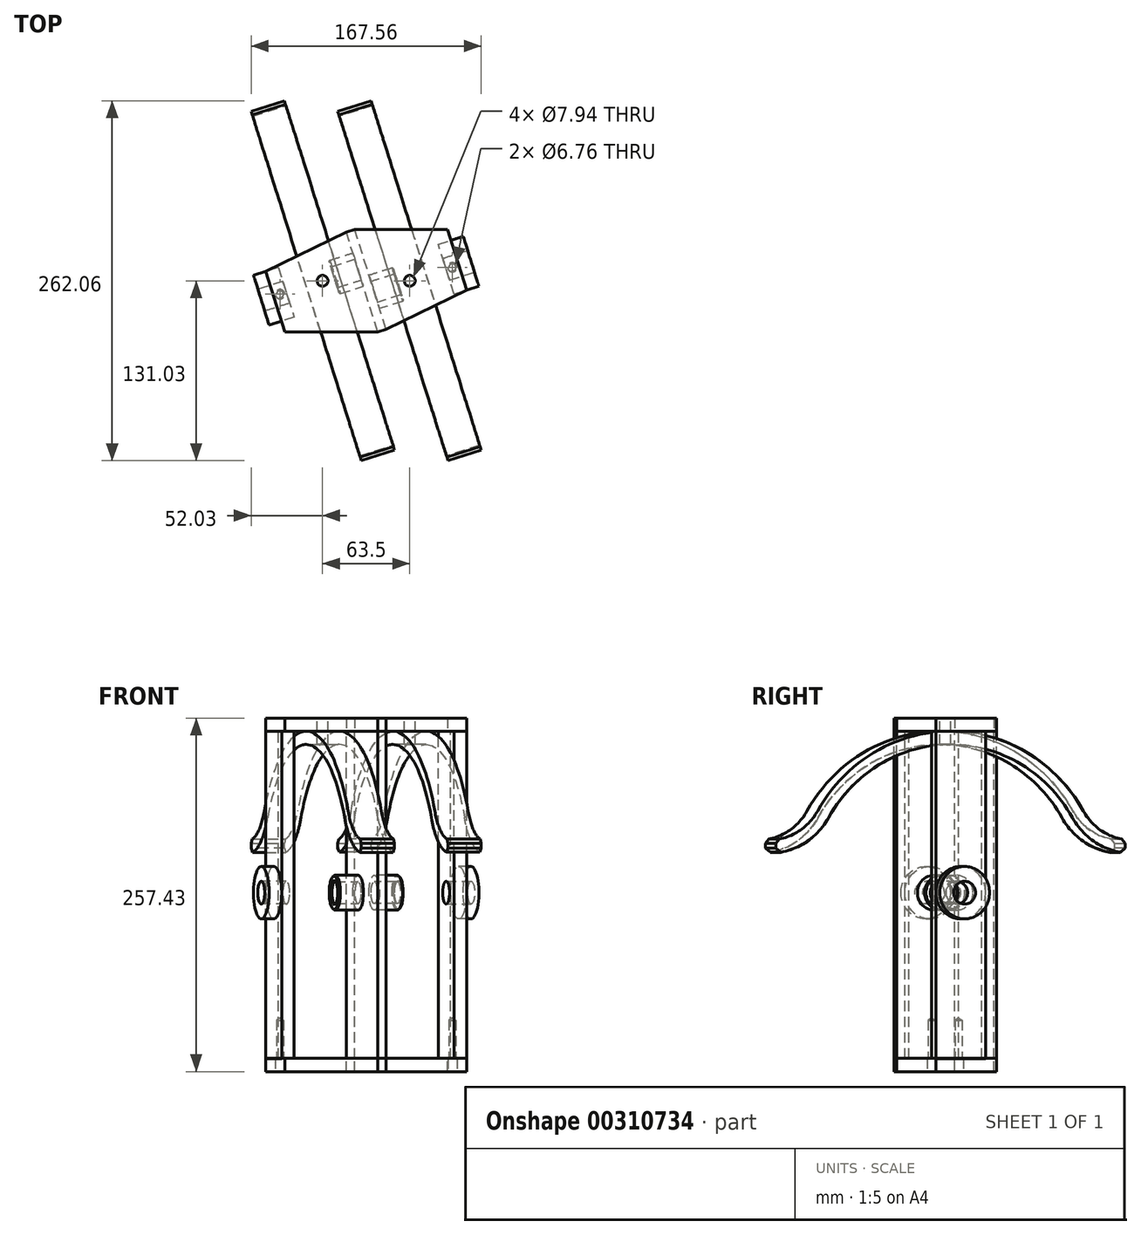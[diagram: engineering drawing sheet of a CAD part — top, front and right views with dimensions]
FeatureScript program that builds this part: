
annotation { "Feature Type Name" : "Feature", "Feature Type Description" : "" }
export const myFeature = defineFeature(function(context is Context, id is Id, definition is map)
    precondition{}
    {
        {
            var Q0;
            Q0=qCreatedBy(makeId("Top.planeOp"),FACE);
            var sketch = newSketch(context, id + "F0", { "sketchPlane" : qUnion([Q0])});
            skLineSegment(sketch, "E0", {"start": v(0, 0) * mm, "end": v(0, 62.19) * mm, "construction": true});
            skLineSegment(sketch, "E1", {"start": v(27.27, -86.5) * mm, "end": v(-20.74, 65.78) * mm, "construction": true});
            skLineSegment(sketch, "E2.0", {"start": v(-45.4, -109.41) * mm, "end": v(-93.41, 42.87) * mm, "construction": true});
            skLineSegment(sketch, "E3.0", {"start": v(14.48, -35.38) * mm, "end": v(-8.43, 37.3) * mm});
            skLineSegment(sketch, "E4", {"start": v(0, 0) * mm, "end": v(58.7, 18.5) * mm, "construction": true});
            skLineSegment(sketch, "E5.0", {"start": v(8.43, -37.3) * mm, "end": v(14.48, -35.38) * mm});
            skLineSegment(sketch, "E6.MirrorCS", {"start": v(-14.48, 35.38) * mm, "end": v(-8.43, 37.3) * mm});
            skLineSegment(sketch, "E7.MirrorCS", {"start": v(8.43, -37.3) * mm, "end": v(-14.48, 35.38) * mm});
            skPoint(sketch, "E8.orphan", {"position": v(-11.46, 36.34) * mm});
            skPoint(sketch, "E9.orphan", {"position": v(11.46, -36.34) * mm});
            skPoint(sketch, "E10.orphan", {"position": v(47.25, 54.85) * mm});
            skPoint(sketch, "E11.orphan", {"position": v(-17.71, 66.74) * mm});
            skPoint(sketch, "E12.orphan", {"position": v(-23.77, 64.83) * mm});
            skPoint(sketch, "E13.orphan", {"position": v(70.16, -17.83) * mm});
            skPoint(sketch, "E14.orphan", {"position": v(30.3, -85.54) * mm});
            skPoint(sketch, "E15.orphan", {"position": v(24.25, -87.45) * mm});
            skSolve(sketch);
        }
        {
            var Q0;
            Q0 = qSketchRegion(id + "F0", true);
            extrude(context, id + "F1", {"entities" : qUnion([Q0]), "oppositeDirection" : true, "depth" : 238.12 * mm});
        }
        {
            var Q0;
            Q0=makeQuery(id+"F1.opExtrude","SWEPT_FACE",FACE,{"disambiguationData":[OSD([sQuery(id+"F0.wireOp",EDGE,"E3.0")])]});
            var sketch = newSketch(context, id + "F2", { "sketchPlane" : qUnion([Q0])});
            skLineSegment(sketch, "E16.0", {"start": v(-38.1, 0) * mm, "end": v(38.1, 0) * mm, "construction": true});
            skLineSegment(sketch, "E17.0", {"start": v(-38.1, -117.48) * mm, "end": v(38.1, -117.48) * mm, "construction": true});
            skLineSegment(sketch, "E18", {"start": v(0, 10.84) * mm, "end": v(0, -152.28) * mm, "construction": true});
            skLineSegment(sketch, "E19.0", {"start": v(-9.53, 10.84) * mm, "end": v(-9.52, -152.28) * mm, "construction": true});
            skCircle(sketch, "E20", {"center": v(-9.52, -117.48) * mm, "radius": 12.7 * mm});
            skCircle(sketch, "E21", {"center": v(-9.52, -117.48) * mm, "radius": 7.94 * mm});
            skSolve(sketch);
        }
        {
            var Q0;
            Q0 = qSketchRegion(id + "F2", true);
            extrude(context, id + "F3", {"entities" : qUnion([Q0]), "operationType" : NewBodyOperationType.ADD, "depth" : 18.29 * mm});
        }
        {
            var Q0;
            Q0=makeQuery(id+"F3.opExtrude","CAP_FACE",FACE,{"disambiguationData":[OSD([sQuery(id+"F2.wireOp",EDGE,"E20"),sQuery(id+"F2.wireOp",EDGE,"E21")])],"isStart":false});
            chamfer(context, id + "F4", {"entities" : qUnion([Q0]), "width" : 0.76 * mm, "tangentPropagation" : true});
        }
        {
            var Q0;
            Q0=makeQuery(id+"F1.opExtrude","SWEPT_FACE",FACE,{"disambiguationData":[OSD([sQuery(id+"F0.wireOp",EDGE,"E7.MirrorCS")])]});
            var sketch = newSketch(context, id + "F5", { "sketchPlane" : qUnion([Q0])});
            skLineSegment(sketch, "E22", {"start": v(0, 41.67) * mm, "end": v(0, -224.56) * mm, "construction": true});
            skCircle(sketch, "E23.0", {"center": v(9.52, -117.48) * mm, "radius": 12.7 * mm, "construction": true});
            skCircle(sketch, "E24.0", {"center": v(9.52, -117.48) * mm, "radius": 7.94 * mm, "construction": true});
            skCircle(sketch, "E25.MirrorC", {"center": v(-9.52, -117.48) * mm, "radius": 12.7 * mm});
            skCircle(sketch, "E26.MirrorC", {"center": v(-9.52, -117.48) * mm, "radius": 7.94 * mm});
            skSolve(sketch);
        }
        {
            var Q0;
            Q0 = qSketchRegion(id + "F5", true);
            extrude(context, id + "F6", {"entities" : qUnion([Q0]), "operationType" : NewBodyOperationType.ADD, "depth" : 18.29 * mm});
        }
        {
            var Q0;
            Q0=makeQuery(id+"F6.opExtrude","CAP_FACE",FACE,{"disambiguationData":[OSD([sQuery(id+"F5.wireOp",EDGE,"E25.MirrorC"),sQuery(id+"F5.wireOp",EDGE,"E26.MirrorC")])],"isStart":false});
            chamfer(context, id + "F7", {"entities" : qUnion([Q0]), "width" : 0.76 * mm, "tangentPropagation" : true});
        }
        {
            var Q0;
            Q0=makeQuery(id+"F1.opExtrude","CAP_FACE",FACE,{"disambiguationData":[OSD([sQuery(id+"F0.wireOp",EDGE,"E3.0"),sQuery(id+"F0.wireOp",EDGE,"E5.0"),sQuery(id+"F0.wireOp",EDGE,"E6.MirrorCS"),sQuery(id+"F0.wireOp",EDGE,"E7.MirrorCS")])],"isStart":true});
            var sketch = newSketch(context, id + "F8", { "sketchPlane" : qUnion([Q0])});
            skLineSegment(sketch, "E27.0.0", {"start": v(-14.48, 35.38) * mm, "end": v(8.43, -37.3) * mm, "construction": true});
            skLineSegment(sketch, "E27.0.1", {"start": v(8.43, -37.3) * mm, "end": v(14.48, -35.38) * mm, "construction": true});
            skLineSegment(sketch, "E27.0.2", {"start": v(14.48, -35.38) * mm, "end": v(-8.43, 37.3) * mm, "construction": true});
            skLineSegment(sketch, "E27.0.3", {"start": v(-8.43, 37.3) * mm, "end": v(-14.48, 35.38) * mm, "construction": true});
            skLineSegment(sketch, "E28.0", {"start": v(63.95, -9.8) * mm, "end": v(52.49, 26.54) * mm});
            skLineSegment(sketch, "E29.0", {"start": v(73.03, -6.94) * mm, "end": v(61.57, 29.4) * mm});
            skLineSegment(sketch, "E30", {"start": v(3.59, 4.46) * mm, "end": v(18.85, 9.27) * mm, "construction": true});
            skLineSegment(sketch, "E31", {"start": v(26.49, -14.95) * mm, "end": v(11.23, -19.76) * mm, "construction": true});
            skLineSegment(sketch, "E32", {"start": v(11.22, 6.87) * mm, "end": v(18.86, -17.36) * mm, "construction": true});
            skLineSegment(sketch, "E33", {"start": v(15.04, -5.25) * mm, "end": v(104, 22.8) * mm, "construction": true});
            skLineSegment(sketch, "E34.0", {"start": v(63.95, -9.8) * mm, "end": v(73.03, -6.94) * mm});
            skLineSegment(sketch, "E35.MirrorCS", {"start": v(52.49, 26.54) * mm, "end": v(61.57, 29.4) * mm});
            skPoint(sketch, "E36.orphan", {"position": v(9.3, 12.92) * mm});
            skPoint(sketch, "E37.orphan", {"position": v(20.77, -23.41) * mm});
            skPoint(sketch, "E38.orphan", {"position": v(98.28, 40.97) * mm});
            skPoint(sketch, "E39.orphan", {"position": v(109.74, 4.64) * mm});
            skLineSegment(sketch, "E40.0", {"start": v(-63.95, 9.8) * mm, "end": v(-52.49, -26.54) * mm});
            skLineSegment(sketch, "E41", {"start": v(-26.49, 14.95) * mm, "end": v(-11.23, 19.76) * mm, "construction": true});
            skLineSegment(sketch, "E42", {"start": v(-3.59, -4.46) * mm, "end": v(-18.85, -9.27) * mm, "construction": true});
            skLineSegment(sketch, "E43", {"start": v(-18.86, 17.36) * mm, "end": v(-11.22, -6.87) * mm, "construction": true});
            skLineSegment(sketch, "E44", {"start": v(-15.04, 5.25) * mm, "end": v(-81.51, -15.71) * mm, "construction": true});
            skLineSegment(sketch, "E45.0", {"start": v(-73.03, 6.94) * mm, "end": v(-61.57, -29.4) * mm});
            skLineSegment(sketch, "E46.0", {"start": v(-63.95, 9.8) * mm, "end": v(-73.03, 6.94) * mm});
            skLineSegment(sketch, "E47.MirrorCS", {"start": v(-52.49, -26.54) * mm, "end": v(-61.57, -29.4) * mm});
            skPoint(sketch, "E48.orphan", {"position": v(-20.77, 23.41) * mm});
            skPoint(sketch, "E49.orphan", {"position": v(-9.3, -12.92) * mm});
            skPoint(sketch, "E50.orphan", {"position": v(-75.78, -33.88) * mm});
            skPoint(sketch, "E51.orphan", {"position": v(-87.24, 2.45) * mm});
            skSolve(sketch);
        }
        {
            var Q0;
            Q0=makeQuery(id+"F8.imprint","IMPRINT",FACE,{"disambiguationData":[TD([[makeQuery(id+"F8.imprint","IMPRINT",EDGE,{"derivedFrom":sQuery(id+"F8.wireOp",EDGE,"E40.0")}),-1.0]])]});
            var Q1;
            Q1=makeQuery(id+"F8.imprint","IMPRINT",FACE,{"disambiguationData":[TD([[makeQuery(id+"F8.imprint","IMPRINT",EDGE,{"derivedFrom":sQuery(id+"F8.wireOp",EDGE,"E28.0")}),-1.0]])]});
            var Q2;
            Q2 = qConstructionFilter(qBodyType(qCreatedBy(id + "F8" ,EDGE), BodyType.WIRE), ConstructionObject.NO);
            extrude(context, id + "F9", {"entities" : qUnion([Q0, Q1]), "surfaceEntities" : qUnion([Q2]), "oppositeDirection" : true, "depth" : 238.25 * mm});
        }
        {
            var Q0;
            Q0=makeQuery(id+"F9.opExtrude","SWEPT_FACE",FACE,{"disambiguationData":[OSD([sQuery(id+"F8.wireOp",EDGE,"E29.0")])]});
            var sketch = newSketch(context, id + "F10", { "sketchPlane" : qUnion([Q0])});
            skCircle(sketch, "E52.0.0", {"center": v(-9.52, -117.48) * mm, "radius": 11.94 * mm, "construction": true});
            skSolve(sketch);
        }
        {
            var Q0;
            Q0=sQuery(id+"F10.wireOp",VERTEX,"E52.0.0.center");
            var Q1;
            Q1=makeQuery(id+"F9.opExtrude","SWEPT_BODY",BODY,{"disambiguationData":[OSD([sQuery(id+"F8.wireOp",EDGE,"E28.0"),sQuery(id+"F8.wireOp",EDGE,"E29.0"),sQuery(id+"F8.wireOp",EDGE,"E34.0"),sQuery(id+"F8.wireOp",EDGE,"E35.MirrorCS")])]});
            hole(context, id + "F11", {"style" : HoleStyle.SIMPLE, "endStyle" : HoleEndStyle.BLIND, "standardTappedOrClearance" : lookupTablePath({ "standard" : "ANSI", "engagement" : "75%", "pitch" : "10 tpi", "size" : "3/4", "type" : "Tapped" }), "standardBlindInLast" : lookupTablePath({ "standard" : "ANSI", "engagement" : "75%", "pitch" : "10 tpi", "size" : "3/4", "type" : "Tapped" }), "holeDiameter" : 16.67 * mm, "showTappedDepth" : true, "holeDepth" : 31.75 * mm, "tappedDepth" : 24.13 * mm, "tapClearance" : 3, "startFromSketch" : true, "locations" : qUnion([Q0]), "scope" : qUnion([Q1]), "majorDiameter" : 19.05 * mm});
        }
        {
            var Q0;
            Q0=makeQuery(id+"F9.opExtrude","SWEPT_FACE",FACE,{"disambiguationData":[OSD([sQuery(id+"F8.wireOp",EDGE,"E45.0")])]});
            var sketch = newSketch(context, id + "F12", { "sketchPlane" : qUnion([Q0])});
            skCircle(sketch, "E53.0.0", {"center": v(-9.52, -117.48) * mm, "radius": 11.94 * mm, "construction": true});
            skSolve(sketch);
        }
        {
            var Q0;
            Q0=sQuery(id+"F12.wireOp",VERTEX,"E53.0.0.center");
            var Q1;
            Q1=makeQuery(id+"F9.opExtrude","SWEPT_BODY",BODY,{"disambiguationData":[OSD([sQuery(id+"F8.wireOp",EDGE,"E40.0"),sQuery(id+"F8.wireOp",EDGE,"E45.0"),sQuery(id+"F8.wireOp",EDGE,"E46.0"),sQuery(id+"F8.wireOp",EDGE,"E47.MirrorCS")])]});
            hole(context, id + "F13", {"style" : HoleStyle.SIMPLE, "endStyle" : HoleEndStyle.BLIND, "standardTappedOrClearance" : lookupTablePath({ "standard" : "ANSI", "engagement" : "75%", "pitch" : "10 tpi", "size" : "3/4", "type" : "Tapped" }), "standardBlindInLast" : lookupTablePath({ "standard" : "ANSI", "engagement" : "75%", "pitch" : "10 tpi", "size" : "3/4", "type" : "Tapped" }), "holeDiameter" : 16.67 * mm, "showTappedDepth" : true, "holeDepth" : 31.75 * mm, "tappedDepth" : 24.13 * mm, "tapClearance" : 3, "startFromSketch" : true, "locations" : qUnion([Q0]), "scope" : qUnion([Q1]), "majorDiameter" : 19.05 * mm});
        }
        {
            var Q0;
            Q0=makeQuery(id+"F1.opExtrude","CAP_FACE",FACE,{"disambiguationData":[OSD([sQuery(id+"F0.wireOp",EDGE,"E3.0"),sQuery(id+"F0.wireOp",EDGE,"E5.0"),sQuery(id+"F0.wireOp",EDGE,"E6.MirrorCS"),sQuery(id+"F0.wireOp",EDGE,"E7.MirrorCS")])],"isStart":true});
            var sketch = newSketch(context, id + "F14", { "sketchPlane" : qUnion([Q0])});
            skLineSegment(sketch, "E54.0.1", {"start": v(8.43, -37.3) * mm, "end": v(14.48, -35.38) * mm});
            skLineSegment(sketch, "E54.0.3", {"start": v(-8.43, 37.3) * mm, "end": v(-14.48, 35.38) * mm});
            skLineSegment(sketch, "E55.0.1", {"start": v(-73.03, 6.94) * mm, "end": v(-59.08, -37.3) * mm});
            skLineSegment(sketch, "E56.0.1", {"start": v(73.03, -6.94) * mm, "end": v(59.08, 37.3) * mm});
            skPoint(sketch, "E55.0.3.end.orphan", {"position": v(-63.95, 9.8) * mm});
            skPoint(sketch, "E55.0.2.end.orphan", {"position": v(-52.49, -26.54) * mm});
            skPoint(sketch, "E56.0.3.end.orphan", {"position": v(63.95, -9.8) * mm});
            skPoint(sketch, "E56.0.3.start.orphan", {"position": v(52.49, 26.54) * mm});
            skPoint(sketch, "E57.orphan", {"position": v(-8.43, 37.3) * mm});
            skPoint(sketch, "E58.orphan", {"position": v(-14.48, 35.38) * mm});
            skPoint(sketch, "E59.orphan", {"position": v(8.43, -37.3) * mm});
            skPoint(sketch, "E60.orphan", {"position": v(14.48, -35.38) * mm});
            skPoint(sketch, "E61.orphan", {"position": v(-61.57, -29.4) * mm});
            skPoint(sketch, "E62.orphan", {"position": v(-73.03, 6.94) * mm});
            skPoint(sketch, "E63.orphan", {"position": v(61.57, 29.4) * mm});
            skPoint(sketch, "E64.orphan", {"position": v(73.03, -6.94) * mm});
            skLineSegment(sketch, "E65", {"start": v(14.48, -35.38) * mm, "end": v(73.03, -6.94) * mm});
            skLineSegment(sketch, "E66", {"start": v(-14.48, 35.38) * mm, "end": v(-73.03, 6.94) * mm});
            skLineSegment(sketch, "E67", {"start": v(8.43, -37.3) * mm, "end": v(-59.08, -37.3) * mm});
            skLineSegment(sketch, "E68", {"start": v(-8.43, 37.3) * mm, "end": v(59.08, 37.3) * mm});
            skSolve(sketch);
        }
        {
            var Q0;
            Q0 = qSketchRegion(id + "F14", true);
            extrude(context, id + "F15", {"entities" : qUnion([Q0]), "depth" : 9.65 * mm});
        }
        {
            var Q0;
            Q0=makeQuery(id+"F15.opExtrude","CAP_FACE",FACE,{"disambiguationData":[OSD([sQuery(id+"F14.wireOp",EDGE,"E54.0.1"),sQuery(id+"F14.wireOp",EDGE,"E54.0.3"),sQuery(id+"F14.wireOp",EDGE,"E55.0.1"),sQuery(id+"F14.wireOp",EDGE,"E56.0.1"),sQuery(id+"F14.wireOp",EDGE,"E65"),sQuery(id+"F14.wireOp",EDGE,"E66"),sQuery(id+"F14.wireOp",EDGE,"E67"),sQuery(id+"F14.wireOp",EDGE,"E68")])],"isStart":false});
            var sketch = newSketch(context, id + "F16", { "sketchPlane" : qUnion([Q0])});
            skLineSegment(sketch, "E69", {"start": v(-60.86, 0) * mm, "end": v(-22.5, 0) * mm, "construction": true});
            skLineSegment(sketch, "E70.0", {"start": v(-63.95, 9.8) * mm, "end": v(-52.49, -26.54) * mm, "construction": true});
            skLineSegment(sketch, "E71.0", {"start": v(-19.74, -8.76) * mm, "end": v(-26.92, 14.02) * mm, "construction": true});
            skLineSegment(sketch, "E72.0", {"start": v(19.74, 8.76) * mm, "end": v(26.92, -14.02) * mm, "construction": true});
            skLineSegment(sketch, "E73.0", {"start": v(63.95, -9.8) * mm, "end": v(52.49, 26.54) * mm, "construction": true});
            skLineSegment(sketch, "E74.trimOffspring", {"start": v(22.5, 0) * mm, "end": v(60.86, 0) * mm, "construction": true});
            skPoint(sketch, "E75.orphan", {"position": v(-89.3, 0) * mm});
            skPoint(sketch, "E76", {"position": v(-41.68, 0) * mm});
            skPoint(sketch, "E77", {"position": v(41.68, 0) * mm});
            skLineSegment(sketch, "E78.0", {"start": v(8.43, -37.3) * mm, "end": v(-14.48, 35.38) * mm, "construction": true});
            skLineSegment(sketch, "E79", {"start": v(-9.78, 20.47) * mm, "end": v(-108.3, -10.59) * mm, "construction": true});
            skSolve(sketch);
        }
        {
            var Q0;
            {var subQ1=sQuery(id+"F0.wireOp",EDGE,"E5.0");var subQ2=sQuery(id+"F0.wireOp",EDGE,"E7.MirrorCS");Q0=makeQuery(id+"F6.boolean.opBoolean","SPLIT",FACE,{"disambiguationData":[TD([makeQuery(id+"F1.opExtrude","SWEPT_FACE",FACE,{"disambiguationData":[OSD([subQ1])]})])],"derivedFrom":makeQuery(id+"F1.opExtrude","SWEPT_FACE",FACE,{"disambiguationData":[OSD([subQ2])]})});}
            cPlane(context, id + "F17", {"entities" : qUnion([Q0]), "cplaneType" : CPlaneType.OFFSET, "offset" : 26.92 * mm, "width" : 152.4 * mm, "height" : 152.4 * mm});
        }
        {
            var Q0;
            Q0=qCreatedBy(id+"F17.planeOp",FACE);
            var sketch = newSketch(context, id + "F18", { "sketchPlane" : qUnion([Q0])});
            skCircle(sketch, "E80.0.0", {"center": v(-9.52, -117.48) * mm, "radius": 11.94 * mm, "construction": true});
            skArc(sketch, "E81", {"start": v(83.63, -62.93) * mm, "mid": v(-9.53, -9.53) * mm, "end": v(-102.68, -62.93) * mm});
            skLineSegment(sketch, "E82", {"start": v(-9.52, -117.48) * mm, "end": v(-9.52, -9.53) * mm, "construction": true});
            skLineSegment(sketch, "E83", {"start": v(-9.52, -9.53) * mm, "end": v(-163.72, -9.53) * mm, "construction": true});
            skLineSegment(sketch, "E84.0", {"start": v(104.55, -88.9) * mm, "end": v(-142.88, -88.9) * mm, "construction": true});
            skLineSegment(sketch, "E85.0", {"start": v(-9.52, -36.58) * mm, "end": v(-163.72, -36.58) * mm, "construction": true});
            skLineSegment(sketch, "E86.0", {"start": v(-147.7, -117.48) * mm, "end": v(-147.7, -9.53) * mm, "construction": true});
            skArc(sketch, "E87", {"start": v(-147.7, -88.74) * mm, "mid": v(-121.76, -81.83) * mm, "end": v(-102.68, -62.93) * mm});
            skArc(sketch, "E88", {"start": v(-142.88, -78.82) * mm, "mid": v(-124.5, -72.2) * mm, "end": v(-111.01, -58.06) * mm});
            skArc(sketch, "E89.trimOffspring", {"start": v(-95.54, -37.28) * mm, "mid": v(-95.54, -36.93) * mm, "end": v(-95.53, -36.58) * mm});
            skLineSegment(sketch, "E90.0", {"start": v(-142.88, -88.9) * mm, "end": v(-142.88, -78.82) * mm});
            skLineSegment(sketch, "E91.trimOffspring", {"start": v(-142.88, -36.58) * mm, "end": v(-142.88, -9.53) * mm});
            skLineSegment(sketch, "E92.trimOffspring", {"start": v(-147.7, -88.9) * mm, "end": v(-163.72, -88.9) * mm, "construction": true});
            skLineSegment(sketch, "E93.MirrorCS", {"start": v(123.83, -88.9) * mm, "end": v(123.83, -78.82) * mm});
            skArc(sketch, "E94.MirrorCS", {"start": v(128.65, -88.74) * mm, "mid": v(102.7, -81.83) * mm, "end": v(83.63, -62.93) * mm});
            skLineSegment(sketch, "E95.MirrorCS", {"start": v(128.65, -88.9) * mm, "end": v(144.67, -88.9) * mm, "construction": true});
            skArc(sketch, "E96.MirrorCS", {"start": v(123.83, -78.82) * mm, "mid": v(105.44, -72.2) * mm, "end": v(91.96, -58.06) * mm});
            skArc(sketch, "E97.trimOffspring", {"start": v(91.96, -58.06) * mm, "mid": v(-9.53, 0.13) * mm, "end": v(-111.01, -58.06) * mm});
            skSolve(sketch);
        }
        {
            var Q0;
            Q0 = qSketchRegion(id + "F18", true);
            extrude(context, id + "F19", {"entities" : qUnion([Q0]), "endBound" : BoundingType.SYMMETRIC, "depth" : 25.4 * mm});
        }
        {
            var Q0;
            Q0=makeQuery(id+"F19.opExtrude","SWEPT_EDGE",EDGE,{"disambiguationData":[OSD([sQuery(id+"F18.wireOp",EDGE,"E93.MirrorCS"),sQuery(id+"F18.wireOp",EDGE,"E96.MirrorCS")])]});
            var Q1;
            Q1=makeQuery(id+"F19.opExtrude","SWEPT_EDGE",EDGE,{"disambiguationData":[OSD([sQuery(id+"F18.wireOp",EDGE,"E93.MirrorCS"),sQuery(id+"F18.wireOp",EDGE,"E94.MirrorCS")])]});
            var Q2;
            Q2=makeQuery(id+"F19.opExtrude","SWEPT_EDGE",EDGE,{"disambiguationData":[OSD([sQuery(id+"F18.wireOp",EDGE,"E87"),sQuery(id+"F18.wireOp",EDGE,"E90.0")])]});
            var Q3;
            Q3=makeQuery(id+"F19.opExtrude","SWEPT_EDGE",EDGE,{"disambiguationData":[OSD([sQuery(id+"F18.wireOp",EDGE,"E88"),sQuery(id+"F18.wireOp",EDGE,"E90.0")])]});
            chamfer(context, id + "F20", {"entities" : qUnion([Q0, Q1, Q2, Q3]), "width" : 3.17 * mm, "tangentPropagation" : true});
        }
        {
            var Q0;
            {var subQ1=sQuery(id+"F0.wireOp",EDGE,"E5.0");var subQ3=sQuery(id+"F0.wireOp",EDGE,"E3.0");Q0=makeQuery(id+"F3.boolean.opBoolean","SPLIT",FACE,{"disambiguationData":[TD([makeQuery(id+"F1.opExtrude","SWEPT_FACE",FACE,{"disambiguationData":[OSD([subQ1])]})])],"derivedFrom":makeQuery(id+"F1.opExtrude","SWEPT_FACE",FACE,{"disambiguationData":[OSD([subQ3])]})});}
            cPlane(context, id + "F21", {"entities" : qUnion([Q0]), "cplaneType" : CPlaneType.OFFSET, "offset" : 26.92 * mm, "width" : 152.4 * mm, "height" : 152.4 * mm});
        }
        {
            var Q0;
            Q0=qCreatedBy(id+"F21.planeOp",FACE);
            var sketch = newSketch(context, id + "F22", { "sketchPlane" : qUnion([Q0])});
            skCircle(sketch, "E98.0", {"center": v(-9.52, -117.48) * mm, "radius": 12.7 * mm, "construction": true});
            skArc(sketch, "E99", {"start": v(83.61, -62.9) * mm, "mid": v(-9.52, -9.52) * mm, "end": v(-102.66, -62.9) * mm});
            skArc(sketch, "E100.0", {"start": v(104.55, -88.9) * mm, "mid": v(103.58, -85.27) * mm, "end": v(102.5, -81.68) * mm});
            skLineSegment(sketch, "E101", {"start": v(-9.52, -117.48) * mm, "end": v(-9.52, -9.53) * mm, "construction": true});
            skLineSegment(sketch, "E102", {"start": v(-9.52, -9.53) * mm, "end": v(180.2, -9.53) * mm, "construction": true});
            skLineSegment(sketch, "E103.0", {"start": v(-9.52, -88.9) * mm, "end": v(180.2, -88.9) * mm, "construction": true});
            skLineSegment(sketch, "E104.0", {"start": v(-9.52, -36.5) * mm, "end": v(180.2, -36.5) * mm, "construction": true});
            skLineSegment(sketch, "E105.0", {"start": v(128.65, -117.48) * mm, "end": v(128.65, -9.53) * mm, "construction": true});
            skArc(sketch, "E106", {"start": v(173.35, -9.53) * mm, "mid": v(114.3, 13.7) * mm, "end": v(76.45, -37.24) * mm});
            skArc(sketch, "E107", {"start": v(171.2, -36.5) * mm, "mid": v(142.97, 3.57) * mm, "end": v(95.74, -9.53) * mm});
            skLineSegment(sketch, "E108.0", {"start": v(123.83, -117.48) * mm, "end": v(123.83, -9.53) * mm});
            skArc(sketch, "E109.trimOffspring", {"start": v(91.94, -58.01) * mm, "mid": v(105.43, -72.16) * mm, "end": v(123.83, -78.78) * mm});
            skArc(sketch, "E110.trimOffspring", {"start": v(83.61, -62.9) * mm, "mid": v(102.7, -81.8) * mm, "end": v(128.65, -88.7) * mm});
            skArc(sketch, "E111.MirrorCS", {"start": v(-110.99, -58.01) * mm, "mid": v(-124.48, -72.16) * mm, "end": v(-142.88, -78.78) * mm});
            skArc(sketch, "E112.MirrorCS", {"start": v(-102.66, -62.9) * mm, "mid": v(-119.68, -80.55) * mm, "end": v(-142.88, -88.48) * mm});
            skLineSegment(sketch, "E113.MirrorCS", {"start": v(-142.88, -88.48) * mm, "end": v(-142.88, -78.78) * mm});
            skPoint(sketch, "E114.orphan", {"position": v(-142.88, -9.53) * mm});
            skPoint(sketch, "E115.orphan", {"position": v(-147.7, -88.7) * mm});
            skPoint(sketch, "E116.orphan", {"position": v(-142.88, -117.48) * mm});
            skArc(sketch, "E117.trimOffspring", {"start": v(91.94, -58.01) * mm, "mid": v(-9.52, 0.13) * mm, "end": v(-110.99, -58.01) * mm});
            skSolve(sketch);
        }
        {
            var Q0;
            Q0 = qSketchRegion(id + "F22", true);
            extrude(context, id + "F23", {"entities" : qUnion([Q0]), "endBound" : BoundingType.SYMMETRIC, "depth" : 25.4 * mm});
        }
        {
            var Q0;
            Q0=makeQuery(id+"F23.opExtrude","SWEPT_EDGE",EDGE,{"disambiguationData":[OSD([sQuery(id+"F22.wireOp",EDGE,"E108.0"),sQuery(id+"F22.wireOp",EDGE,"E109.trimOffspring")])]});
            var Q1;
            Q1=makeQuery(id+"F23.opExtrude","SWEPT_EDGE",EDGE,{"disambiguationData":[OSD([sQuery(id+"F22.wireOp",EDGE,"E108.0"),sQuery(id+"F22.wireOp",EDGE,"E110.trimOffspring")])]});
            var Q2;
            Q2=makeQuery(id+"F23.opExtrude","SWEPT_EDGE",EDGE,{"disambiguationData":[OSD([sQuery(id+"F22.wireOp",EDGE,"E111.MirrorCS"),sQuery(id+"F22.wireOp",EDGE,"E113.MirrorCS")])]});
            var Q3;
            Q3=makeQuery(id+"F23.opExtrude","SWEPT_EDGE",EDGE,{"disambiguationData":[OSD([sQuery(id+"F22.wireOp",EDGE,"E112.MirrorCS"),sQuery(id+"F22.wireOp",EDGE,"E113.MirrorCS")])]});
            chamfer(context, id + "F24", {"entities" : qUnion([Q0, Q1, Q2, Q3]), "width" : 3.17 * mm, "tangentPropagation" : true});
        }
        {
            var Q0;
            Q0=makeQuery(id+"F1.opExtrude","CAP_FACE",FACE,{"disambiguationData":[OSD([sQuery(id+"F0.wireOp",EDGE,"E3.0"),sQuery(id+"F0.wireOp",EDGE,"E5.0"),sQuery(id+"F0.wireOp",EDGE,"E6.MirrorCS"),sQuery(id+"F0.wireOp",EDGE,"E7.MirrorCS")])],"isStart":false});
            var sketch = newSketch(context, id + "F25", { "sketchPlane" : qUnion([Q0])});
            skLineSegment(sketch, "E118.0.0", {"start": v(-59.08, 37.3) * mm, "end": v(8.43, 37.3) * mm});
            skLineSegment(sketch, "E118.0.1", {"start": v(8.43, 37.3) * mm, "end": v(14.48, 35.38) * mm});
            skLineSegment(sketch, "E118.0.2", {"start": v(14.48, 35.38) * mm, "end": v(73.03, 6.94) * mm});
            skLineSegment(sketch, "E118.0.3", {"start": v(73.03, 6.94) * mm, "end": v(59.08, -37.3) * mm});
            skLineSegment(sketch, "E118.0.4", {"start": v(59.08, -37.3) * mm, "end": v(-8.43, -37.3) * mm});
            skLineSegment(sketch, "E118.0.5", {"start": v(-8.43, -37.3) * mm, "end": v(-14.48, -35.38) * mm});
            skLineSegment(sketch, "E118.0.6", {"start": v(-14.48, -35.38) * mm, "end": v(-73.03, -6.94) * mm});
            skLineSegment(sketch, "E118.0.7", {"start": v(-73.03, -6.94) * mm, "end": v(-59.08, 37.3) * mm});
            skSolve(sketch);
        }
        {
            var Q0;
            Q0 = qSketchRegion(id + "F25", true);
            extrude(context, id + "F26", {"entities" : qUnion([Q0]), "depth" : 9.65 * mm});
        }
        {
            var Q0;
            Q0=makeQuery(id+"F9.opExtrude","CAP_FACE",FACE,{"disambiguationData":[OSD([sQuery(id+"F8.wireOp",EDGE,"E40.0"),sQuery(id+"F8.wireOp",EDGE,"E45.0"),sQuery(id+"F8.wireOp",EDGE,"E46.0"),sQuery(id+"F8.wireOp",EDGE,"E47.MirrorCS")])],"isStart":false});
            var sketch = newSketch(context, id + "F27", { "sketchPlane" : qUnion([Q0])});
            skLineSegment(sketch, "E119.0.0", {"start": v(-73.03, -6.94) * mm, "end": v(-63.95, -9.8) * mm, "construction": true});
            skLineSegment(sketch, "E119.0.1", {"start": v(-63.95, -9.8) * mm, "end": v(-52.49, 26.54) * mm, "construction": true});
            skLineSegment(sketch, "E119.0.2", {"start": v(-52.49, 26.54) * mm, "end": v(-61.57, 29.4) * mm, "construction": true});
            skLineSegment(sketch, "E119.0.3", {"start": v(-61.57, 29.4) * mm, "end": v(-73.03, -6.94) * mm, "construction": true});
            skLineSegment(sketch, "E120", {"start": v(-73.03, -6.94) * mm, "end": v(-52.49, 26.54) * mm, "construction": true});
            skPoint(sketch, "E121", {"position": v(-62.76, 9.8) * mm});
            skSolve(sketch);
        }
        {
            var Q0;
            Q0=sQuery(id+"F27.wireOp",VERTEX,"E121");
            var Q1;
            Q1=makeQuery(id+"F9.opExtrude","SWEPT_BODY",BODY,{"disambiguationData":[OSD([sQuery(id+"F8.wireOp",EDGE,"E40.0"),sQuery(id+"F8.wireOp",EDGE,"E45.0"),sQuery(id+"F8.wireOp",EDGE,"E46.0"),sQuery(id+"F8.wireOp",EDGE,"E47.MirrorCS")])]});
            hole(context, id + "F28", {"style" : HoleStyle.SIMPLE, "endStyle" : HoleEndStyle.BLIND, "standardTappedOrClearance" : lookupTablePath({ "standard" : "ANSI", "engagement" : "75%", "pitch" : "20 tpi", "size" : "1/4", "type" : "Tapped" }), "standardBlindInLast" : lookupTablePath({ "standard" : "ANSI", "engagement" : "75%", "pitch" : "20 tpi", "size" : "1/4", "type" : "Tapped" }), "holeDiameter" : 5.1 * mm, "showTappedDepth" : true, "holeDepth" : 27.94 * mm, "tappedDepth" : 24.13 * mm, "tapClearance" : 3, "startFromSketch" : true, "locations" : qUnion([Q0]), "scope" : qUnion([Q1]), "majorDiameter" : 6.35 * mm});
        }
        {
            var Q0;
            Q0=makeQuery(id+"F9.opExtrude","CAP_FACE",FACE,{"disambiguationData":[OSD([sQuery(id+"F8.wireOp",EDGE,"E28.0"),sQuery(id+"F8.wireOp",EDGE,"E29.0"),sQuery(id+"F8.wireOp",EDGE,"E34.0"),sQuery(id+"F8.wireOp",EDGE,"E35.MirrorCS")])],"isStart":false});
            var sketch = newSketch(context, id + "F29", { "sketchPlane" : qUnion([Q0])});
            skLineSegment(sketch, "E122.0.0", {"start": v(73.03, 6.94) * mm, "end": v(63.95, 9.8) * mm, "construction": true});
            skLineSegment(sketch, "E122.0.1", {"start": v(63.95, 9.8) * mm, "end": v(52.49, -26.54) * mm, "construction": true});
            skLineSegment(sketch, "E122.0.2", {"start": v(52.49, -26.54) * mm, "end": v(61.57, -29.4) * mm, "construction": true});
            skLineSegment(sketch, "E122.0.3", {"start": v(61.57, -29.4) * mm, "end": v(73.03, 6.94) * mm, "construction": true});
            skLineSegment(sketch, "E123", {"start": v(61.57, -29.4) * mm, "end": v(63.95, 9.8) * mm, "construction": true});
            skPoint(sketch, "E124", {"position": v(62.76, -9.8) * mm});
            skSolve(sketch);
        }
        {
            var Q0;
            Q0=sQuery(id+"F29.wireOp",VERTEX,"E124");
            var Q1;
            Q1=makeQuery(id+"F9.opExtrude","SWEPT_BODY",BODY,{"disambiguationData":[OSD([sQuery(id+"F8.wireOp",EDGE,"E28.0"),sQuery(id+"F8.wireOp",EDGE,"E29.0"),sQuery(id+"F8.wireOp",EDGE,"E34.0"),sQuery(id+"F8.wireOp",EDGE,"E35.MirrorCS")])]});
            hole(context, id + "F30", {"style" : HoleStyle.SIMPLE, "endStyle" : HoleEndStyle.BLIND, "standardTappedOrClearance" : lookupTablePath({ "standard" : "ANSI", "engagement" : "75%", "pitch" : "20 tpi", "size" : "1/4", "type" : "Tapped" }), "standardBlindInLast" : lookupTablePath({ "standard" : "ANSI", "engagement" : "75%", "pitch" : "20 tpi", "size" : "1/4", "type" : "Tapped" }), "holeDiameter" : 5.1 * mm, "showTappedDepth" : true, "holeDepth" : 27.94 * mm, "tappedDepth" : 24.13 * mm, "tapClearance" : 3, "startFromSketch" : true, "locations" : qUnion([Q0]), "scope" : qUnion([Q1]), "majorDiameter" : 6.35 * mm});
        }
        {
            var Q0;
            Q0=makeQuery(id+"F26.opExtrude","CAP_FACE",FACE,{"disambiguationData":[OSD([sQuery(id+"F25.wireOp",EDGE,"E118.0.0"),sQuery(id+"F25.wireOp",EDGE,"E118.0.1"),sQuery(id+"F25.wireOp",EDGE,"E118.0.2"),sQuery(id+"F25.wireOp",EDGE,"E118.0.3"),sQuery(id+"F25.wireOp",EDGE,"E118.0.4"),sQuery(id+"F25.wireOp",EDGE,"E118.0.5"),sQuery(id+"F25.wireOp",EDGE,"E118.0.6"),sQuery(id+"F25.wireOp",EDGE,"E118.0.7")])],"isStart":false});
            var sketch = newSketch(context, id + "F31", { "sketchPlane" : qUnion([Q0])});
            skCircle(sketch, "E125.0", {"center": v(-62.76, 9.8) * mm, "radius": 2.55 * mm, "construction": true});
            skCircle(sketch, "E126.0", {"center": v(62.76, -9.8) * mm, "radius": 2.55 * mm, "construction": true});
            skSolve(sketch);
        }
        {
            var Q0;
            Q0=sQuery(id+"F31.wireOp",VERTEX,"E126.0.center");
            var Q1;
            Q1=sQuery(id+"F31.wireOp",VERTEX,"E125.0.center");
            var Q2;
            Q2=makeQuery(id+"F26.opExtrude","SWEPT_BODY",BODY,{"disambiguationData":[OSD([sQuery(id+"F25.wireOp",EDGE,"E118.0.0"),sQuery(id+"F25.wireOp",EDGE,"E118.0.1"),sQuery(id+"F25.wireOp",EDGE,"E118.0.2"),sQuery(id+"F25.wireOp",EDGE,"E118.0.3"),sQuery(id+"F25.wireOp",EDGE,"E118.0.4"),sQuery(id+"F25.wireOp",EDGE,"E118.0.5"),sQuery(id+"F25.wireOp",EDGE,"E118.0.6"),sQuery(id+"F25.wireOp",EDGE,"E118.0.7")])]});
            hole(context, id + "F32", {"style" : HoleStyle.SIMPLE, "endStyle" : HoleEndStyle.BLIND, "standardTappedOrClearance" : lookupTablePath({ "standard" : "ANSI", "fit" : "Normal (ASME)", "size" : "1/4", "type" : "Clearance" }), "standardBlindInLast" : lookupTablePath({ "fit" : "Free", "standard" : "ANSI", "size" : "1/4", "type" : "Clearance" }), "holeDiameter" : 6.76 * mm, "holeDepth" : 27.94 * mm, "tappedDepth" : 24.13 * mm, "tapClearance" : 3, "startFromSketch" : true, "locations" : qUnion([Q0, Q1]), "scope" : qUnion([Q2])});
        }
        {
            var Q0;
            Q0=makeQuery(id+"F15.opExtrude","CAP_FACE",FACE,{"disambiguationData":[OSD([sQuery(id+"F14.wireOp",EDGE,"E54.0.1"),sQuery(id+"F14.wireOp",EDGE,"E54.0.3"),sQuery(id+"F14.wireOp",EDGE,"E55.0.1"),sQuery(id+"F14.wireOp",EDGE,"E56.0.1"),sQuery(id+"F14.wireOp",EDGE,"E65"),sQuery(id+"F14.wireOp",EDGE,"E66"),sQuery(id+"F14.wireOp",EDGE,"E67"),sQuery(id+"F14.wireOp",EDGE,"E68")])],"isStart":false});
            var sketch = newSketch(context, id + "F33", { "sketchPlane" : qUnion([Q0])});
            skLineSegment(sketch, "E127", {"start": v(44.88, 0) * mm, "end": v(18.24, 0) * mm, "construction": true});
            skLineSegment(sketch, "E128.0.0", {"start": v(-11.05, 92.91) * mm, "end": v(49.97, -100.62) * mm, "construction": true});
            skLineSegment(sketch, "E128.0.1", {"start": v(49.97, -100.62) * mm, "end": v(74.2, -92.98) * mm, "construction": true});
            skLineSegment(sketch, "E128.0.2", {"start": v(74.2, -92.98) * mm, "end": v(13.17, 100.55) * mm, "construction": true});
            skLineSegment(sketch, "E128.0.3", {"start": v(13.17, 100.55) * mm, "end": v(-11.05, 92.91) * mm, "construction": true});
            skLineSegment(sketch, "E129.0.0", {"start": v(11.06, -92.94) * mm, "end": v(-49.98, 100.64) * mm, "construction": true});
            skLineSegment(sketch, "E129.0.1", {"start": v(-49.98, 100.64) * mm, "end": v(-74.2, 93) * mm, "construction": true});
            skLineSegment(sketch, "E129.0.2", {"start": v(-74.2, 93) * mm, "end": v(-13.16, -100.58) * mm, "construction": true});
            skLineSegment(sketch, "E129.0.3", {"start": v(-13.16, -100.58) * mm, "end": v(11.06, -92.94) * mm, "construction": true});
            skPoint(sketch, "E130.orphan", {"position": v(97.9, 0) * mm});
            skLineSegment(sketch, "E131.trimOffspring", {"start": v(-18.24, 0) * mm, "end": v(-44.88, 0) * mm, "construction": true});
            skPoint(sketch, "E132", {"position": v(31.75, 0) * mm});
            skPoint(sketch, "E133", {"position": v(-31.75, 0) * mm});
            skSolve(sketch);
        }
        {
            var Q0;
            Q0=sQuery(id+"F33.wireOp",VERTEX,"E132");
            var Q1;
            Q1=sQuery(id+"F33.wireOp",VERTEX,"E133");
            var Q2;
            Q2=makeQuery(id+"F15.opExtrude","SWEPT_BODY",BODY,{"disambiguationData":[OSD([sQuery(id+"F14.wireOp",EDGE,"E54.0.1"),sQuery(id+"F14.wireOp",EDGE,"E54.0.3"),sQuery(id+"F14.wireOp",EDGE,"E55.0.1"),sQuery(id+"F14.wireOp",EDGE,"E56.0.1"),sQuery(id+"F14.wireOp",EDGE,"E65"),sQuery(id+"F14.wireOp",EDGE,"E66"),sQuery(id+"F14.wireOp",EDGE,"E67"),sQuery(id+"F14.wireOp",EDGE,"E68")])]});
            var Q3;
            Q3=makeQuery(id+"F19.opExtrude","SWEPT_BODY",BODY,{"disambiguationData":[OSD([sQuery(id+"F18.wireOp",EDGE,"E81"),sQuery(id+"F18.wireOp",EDGE,"E87"),sQuery(id+"F18.wireOp",EDGE,"E88"),sQuery(id+"F18.wireOp",EDGE,"E90.0"),sQuery(id+"F18.wireOp",EDGE,"E93.MirrorCS"),sQuery(id+"F18.wireOp",EDGE,"E94.MirrorCS"),sQuery(id+"F18.wireOp",EDGE,"E96.MirrorCS"),sQuery(id+"F18.wireOp",EDGE,"E97.trimOffspring")])]});
            var Q4;
            Q4=makeQuery(id+"F23.opExtrude","SWEPT_BODY",BODY,{"disambiguationData":[OSD([sQuery(id+"F22.wireOp",EDGE,"E99"),sQuery(id+"F22.wireOp",EDGE,"E108.0"),sQuery(id+"F22.wireOp",EDGE,"E109.trimOffspring"),sQuery(id+"F22.wireOp",EDGE,"E110.trimOffspring"),sQuery(id+"F22.wireOp",EDGE,"E111.MirrorCS"),sQuery(id+"F22.wireOp",EDGE,"E112.MirrorCS"),sQuery(id+"F22.wireOp",EDGE,"E113.MirrorCS"),sQuery(id+"F22.wireOp",EDGE,"E117.trimOffspring")])]});
            hole(context, id + "F34", {"style" : HoleStyle.SIMPLE, "endStyle" : HoleEndStyle.BLIND, "standardTappedOrClearance" : lookupTablePath({ "standard" : "ANSI", "engagement" : "75%", "pitch" : "16 tpi", "size" : "3/8", "type" : "Tapped" }), "standardBlindInLast" : lookupTablePath({ "standard" : "ANSI", "engagement" : "75%", "pitch" : "16 tpi", "size" : "3/8", "type" : "Tapped" }), "holeDiameter" : 7.94 * mm, "showTappedDepth" : true, "holeDepth" : 28.9 * mm, "tappedDepth" : 24.13 * mm, "tapClearance" : 3, "startFromSketch" : true, "locations" : qUnion([Q0, Q1]), "scope" : qUnion([Q2, Q3, Q4]), "majorDiameter" : 9.53 * mm});
        }
        {
            var Q0;
            Q0=makeQuery(id+"F9.opExtrude","SWEPT_FACE",FACE,{"disambiguationData":[OSD([sQuery(id+"F8.wireOp",EDGE,"E29.0")])]});
            var sketch = newSketch(context, id + "F35", { "sketchPlane" : qUnion([Q0])});
            skSolve(sketch);
        }
        {
            var Q0;
            {var subQ0=sQuery(id+"F8.wireOp",EDGE,"E29.0");Q0=makeQuery(id+"F35.imprint","IMPRINT",FACE,{"disambiguationData":[TD([[makeQuery(id+"F35.imprint","IMPRINT",EDGE,{"derivedFrom":makeQuery(id+"F9.opExtrude","CAP_EDGE",EDGE,{"disambiguationData":[OSD([subQ0])],"isStart":true})}),-1.0]])]});}
            var sketch = newSketch(context, id + "F36", { "sketchPlane" : qUnion([Q0])});
            skCircle(sketch, "E134.0.0", {"center": v(-9.52, -117.48) * mm, "radius": 8.33 * mm});
            skCircle(sketch, "E135", {"center": v(-9.52, -117.48) * mm, "radius": 19.05 * mm});
            skSolve(sketch);
        }
        {
            var Q0;
            Q0 = qSketchRegion(id + "F36", true);
            extrude(context, id + "F37", {"entities" : qUnion([Q0]), "operationType" : NewBodyOperationType.ADD, "depth" : 9.52 * mm});
        }
        {
            var Q0;
            Q0=makeQuery(id+"F9.opExtrude","SWEPT_FACE",FACE,{"disambiguationData":[OSD([sQuery(id+"F8.wireOp",EDGE,"E45.0")])]});
            var sketch = newSketch(context, id + "F38", { "sketchPlane" : qUnion([Q0])});
            skCircle(sketch, "E136.0", {"center": v(-9.52, -117.48) * mm, "radius": 8.33 * mm});
            skCircle(sketch, "E137", {"center": v(-9.52, -117.48) * mm, "radius": 19.05 * mm});
            skSolve(sketch);
        }
        {
            var Q0;
            Q0 = qSketchRegion(id + "F38", true);
            extrude(context, id + "F39", {"entities" : qUnion([Q0]), "operationType" : NewBodyOperationType.ADD, "depth" : 9.52 * mm});
        }
    });
